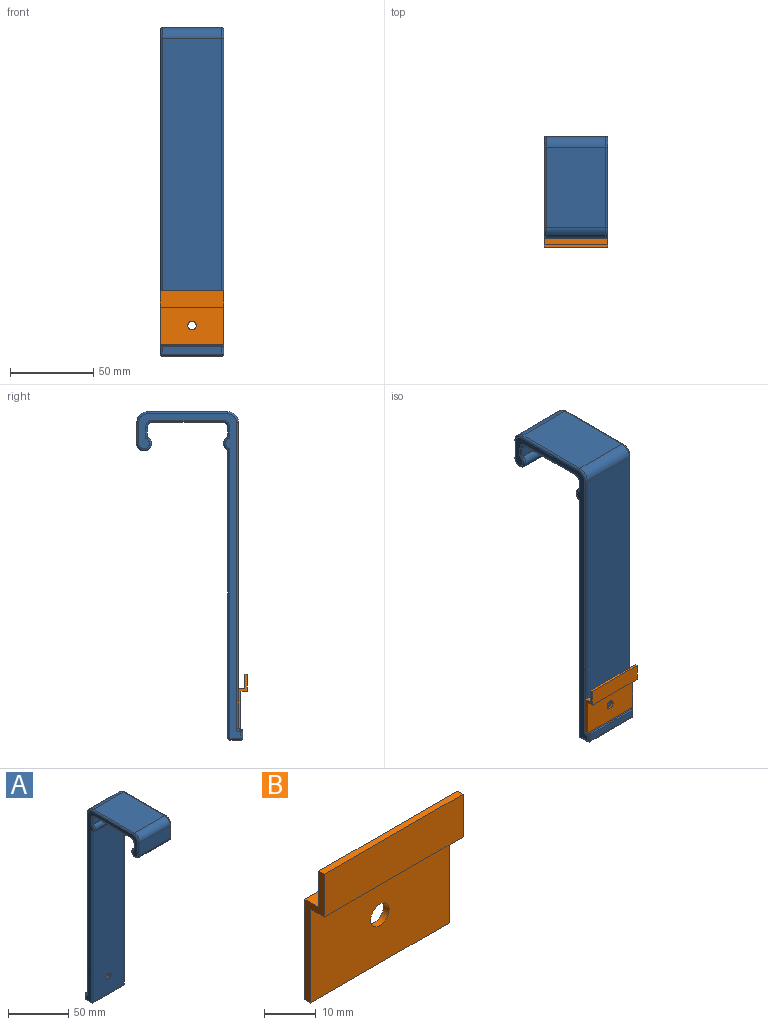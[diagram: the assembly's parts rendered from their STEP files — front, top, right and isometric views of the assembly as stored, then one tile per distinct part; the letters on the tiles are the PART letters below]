
ASSEMBLY  parts=2 mates=1
PART A: 74 faces, bbox 38.1x64x197.4 mm
  f0: plane 35.56x12.7mm, normal (0,-1,0), area 451.6mm2, adj f1,f22,f43,f66
  f1: cylinder r=4.45mm len=35.56mm, axis (-1,0,0), area 662.1mm2, adj f0,f2,f41,f64
  f2: cylinder r=0.64mm len=35.56mm, axis (-1,0,0), area 23.6mm2, adj f1,f3,f39,f62
  f3: plane 35.56x5.13mm, normal (0,1,0), area 182.3mm2, adj f2,f4,f37,f60
  f4: cylinder r=3.17mm len=35.56mm, axis (-1,0,0), area 177.3mm2, adj f3,f5,f35,f58
  f5: plane 41.91x35.56mm, normal (0,0,-1), area 1490.3mm2, adj f4,f6,f33,f56
  f6: cylinder r=3.17mm len=35.56mm, axis (-1,0,0), area 177.3mm2, adj f5,f7,f31,f54
  f7: plane 35.56x5.13mm, normal (0,-1,0), area 182.3mm2, adj f6,f8,f29,f52
  f8: cylinder r=0.64mm len=35.56mm, axis (-1,0,0), area 23.6mm2, adj f7,f9,f27,f50
  f9: cylinder r=4.45mm len=35.56mm, axis (-1,0,0), area 331mm2, adj f8,f10,f25,f48
  f10: cylinder r=0.64mm len=35.56mm, axis (-1,0,0), area 23.6mm2, adj f9,f11,f26,f49
  f11: plane 172.13x35.56mm, normal (0,-1,0), area 6089.3mm2, adj f10,f12,f28,f51,f72
  f12: cylinder r=1.27mm len=35.56mm, axis (-1,0,0), area 70.9mm2, adj f11,f13,f30,f53
  f13: plane 35.56x6.35mm, normal (0,0,-1), area 225.8mm2, adj f12,f14,f32,f55
  f14: cylinder r=1.27mm len=35.56mm, axis (-1,0,0), area 70.9mm2, adj f13,f15,f34,f57
  f15: plane 35.56x4.45mm, normal (0,1,0), area 158.1mm2, adj f14,f16,f36,f59
  f16: cylinder r=0.64mm len=35.56mm, axis (-1,0,0), area 35.5mm2, adj f15,f17,f38,f61
  f17: plane 35.56x1.27mm, normal (0,0,1), area 45.2mm2, adj f16,f18,f40,f63
  f18: cylinder r=0.64mm len=35.56mm, axis (-1,0,0), area 35.5mm2, adj f17,f19,f42,f65
  f19: plane 183.52x35.56mm, normal (0,1,0), area 6494.1mm2, adj f18,f20,f44,f67,f73
  f20: cylinder r=6.35mm len=35.56mm, axis (-1,0,0), area 354.7mm2, adj f19,f21,f46,f69
  f21: plane 48.26x35.56mm, normal (0,0,1), area 1716.1mm2, adj f20,f22,f47,f70
  f22: cylinder r=6.35mm len=35.56mm, axis (-1,0,0), area 354.7mm2, adj f0,f21,f45,f68
  f23: plane 194.31x60.96mm, normal (1,0,0), area 1043.8mm2, adj f48,f49,f50,f51,f52,f54,f55,f56
  f24: plane 194.31x60.96mm, normal (-1,0,0), area 1043.8mm2, adj f25,f26,f27,f28,f29,f31,f32,f33
  f25: torus R=3.17mm, axis (1,0,0), area 16.6mm2, adj f9,f24,f26,f27
  f26: torus R=1.91mm, axis (1,0,0), area 2.3mm2, adj f10,f24,f25,f28
  f27: torus R=1.91mm, axis (1,0,0), area 2.3mm2, adj f8,f24,f25,f29
  f28: cylinder r=1.27mm len=172.13mm, axis (0,0,-1), area 343.4mm2, adj f11,f24,f26,f30
  f29: cylinder r=1.27mm len=5.13mm, axis (0,0,-1), area 10.2mm2, adj f7,f24,f27,f31
  f30: sphere r=1.27mm, area 2.5mm2, adj f12,f28,f32
  f31: torus R=4.45mm, axis (1,0,0), area 11.4mm2, adj f6,f24,f29,f33
  f32: cylinder r=1.27mm len=6.35mm, axis (0,1,0), area 12.7mm2, adj f13,f24,f30,f34
  f33: cylinder r=1.27mm len=41.91mm, axis (0,1,0), area 83.6mm2, adj f5,f24,f31,f35
  f34: sphere r=1.27mm, area 2.5mm2, adj f14,f32,f36
  f35: torus R=4.45mm, axis (1,0,0), area 11.4mm2, adj f4,f24,f33,f37
  f36: cylinder r=1.27mm len=4.45mm, axis (0,0,1), area 8.4mm2, adj f15,f24,f34,f38
  f37: cylinder r=1.27mm len=5.13mm, axis (0,0,1), area 10.2mm2, adj f3,f24,f35,f39
  f38: bspline ~1.52x1.27mm, area 1.3mm2, adj f16,f36,f40
  f39: torus R=1.91mm, axis (1,0,0), area 2.3mm2, adj f2,f24,f37,f41
  f40: cylinder r=1.27mm len=1.27mm, axis (0,-1,0), area 2.1mm2, adj f17,f24,f38,f42
  f41: torus R=3.17mm, axis (1,0,0), area 33.3mm2, adj f1,f24,f39,f43
  f42: torus R=1.91mm, axis (1,0,0), area 3.4mm2, adj f18,f24,f40,f44
  f43: cylinder r=1.27mm len=12.7mm, axis (0,0,-1), area 25.3mm2, adj f0,f24,f41,f45
  f44: cylinder r=1.27mm len=183.52mm, axis (0,0,1), area 366.1mm2, adj f19,f24,f42,f46
  f45: torus R=5.08mm, axis (1,0,0), area 18.5mm2, adj f22,f24,f43,f47
  f46: torus R=5.08mm, axis (1,0,0), area 18.5mm2, adj f20,f24,f44,f47
  f47: cylinder r=1.27mm len=48.26mm, axis (0,-1,0), area 96.3mm2, adj f21,f24,f45,f46
  f48: torus R=3.17mm, axis (1,0,0), area 16.6mm2, adj f9,f23,f49,f50
  f49: torus R=1.91mm, axis (1,0,0), area 2.3mm2, adj f10,f23,f48,f51
  f50: torus R=1.91mm, axis (1,0,0), area 2.3mm2, adj f8,f23,f48,f52
  f51: cylinder r=1.27mm len=172.13mm, axis (0,0,1), area 343.4mm2, adj f11,f23,f49,f53
  f52: cylinder r=1.27mm len=5.13mm, axis (0,0,1), area 10.2mm2, adj f7,f23,f50,f54
  f53: sphere r=1.27mm, area 2.5mm2, adj f12,f51,f55
  f54: torus R=4.45mm, axis (1,0,0), area 11.4mm2, adj f6,f23,f52,f56
  f55: cylinder r=1.27mm len=6.35mm, axis (0,-1,0), area 12.7mm2, adj f13,f23,f53,f57
  f56: cylinder r=1.27mm len=41.91mm, axis (0,-1,0), area 83.6mm2, adj f5,f23,f54,f58
  f57: sphere r=1.27mm, area 2.5mm2, adj f14,f55,f59
  f58: torus R=4.45mm, axis (1,0,0), area 11.4mm2, adj f4,f23,f56,f60
  f59: cylinder r=1.27mm len=4.45mm, axis (0,0,-1), area 8.4mm2, adj f15,f23,f57,f61
  f60: cylinder r=1.27mm len=5.13mm, axis (0,0,-1), area 10.2mm2, adj f3,f23,f58,f62
  f61: bspline ~1.52x1.27mm, area 1.3mm2, adj f16,f59,f63
  f62: torus R=1.91mm, axis (1,0,0), area 2.3mm2, adj f2,f23,f60,f64
  f63: cylinder r=1.27mm len=1.27mm, axis (0,1,0), area 2.1mm2, adj f17,f23,f61,f65
  f64: torus R=3.17mm, axis (1,0,0), area 33.3mm2, adj f1,f23,f62,f66
  f65: torus R=1.91mm, axis (1,0,0), area 3.4mm2, adj f18,f23,f63,f67
  f66: cylinder r=1.27mm len=12.7mm, axis (0,0,1), area 25.3mm2, adj f0,f23,f64,f68
  f67: cylinder r=1.27mm len=183.52mm, axis (0,0,-1), area 366.1mm2, adj f19,f23,f65,f69
  f68: torus R=5.08mm, axis (1,0,0), area 18.5mm2, adj f22,f23,f66,f70
  f69: torus R=5.08mm, axis (1,0,0), area 18.5mm2, adj f20,f23,f67,f70
  f70: cylinder r=1.27mm len=48.26mm, axis (0,1,0), area 96.3mm2, adj f21,f23,f68,f69
  f71: cylinder r=2.54mm len=5.08mm, axis (0,1,0), area 81.1mm2, adj f72,f73
  f72: cone r=3.17mm half-angle=45deg, axis (0,-1,0), area 16.1mm2, adj f11,f71
  f73: cone r=2.54mm half-angle=45deg, axis (0,1,0), area 16.1mm2, adj f19,f71
PART B: 11 faces, bbox 38.1x5.3x32.5 mm
  f0: plane 38.1x3.81mm, normal (0,0,1), area 145.2mm2, adj f1,f7,f8,f9
  f1: plane 38.1x8.64mm, normal (0,1,0), area 329mm2, adj f0,f2,f8,f9
  f2: plane 38.1x1.52mm, normal (0,0,1), area 58.1mm2, adj f1,f3,f8,f9
  f3: plane 38.1x10.16mm, normal (0,-1,0), area 387.1mm2, adj f2,f4,f8,f9
  f4: plane 38.1x3.81mm, normal (0,0,-1), area 145.2mm2, adj f3,f5,f8,f9
  f5: plane 38.1x22.35mm, normal (0,-1,0), area 831.3mm2, adj f4,f6,f8,f9,f10
  f6: plane 38.1x1.52mm, normal (0,0,-1), area 58.1mm2, adj f5,f7,f8,f9
  f7: plane 38.1x23.88mm, normal (0,1,0), area 889.4mm2, adj f0,f6,f8,f9,f10
  f8: plane 32.51x5.33mm, normal (1,0,0), area 55.4mm2, adj f0,f1,f2,f3,f4,f5,f6,f7
  f9: plane 32.51x5.33mm, normal (-1,0,0), area 55.4mm2, adj f0,f1,f2,f3,f4,f5,f6,f7
  f10: cylinder r=2.54mm len=5.08mm, axis (0,1,0), area 24.3mm2, adj f5,f7
PLACE A rot(axis=(0,0,1),180deg) t=(0,-30.48,6.35)mm
PLACE B t=(0,-30.48,-159.64)mm
MATE fastened B.f10 <-> A.f72  axis (0,1,0) through (0,-30.48,-172.08)mm
